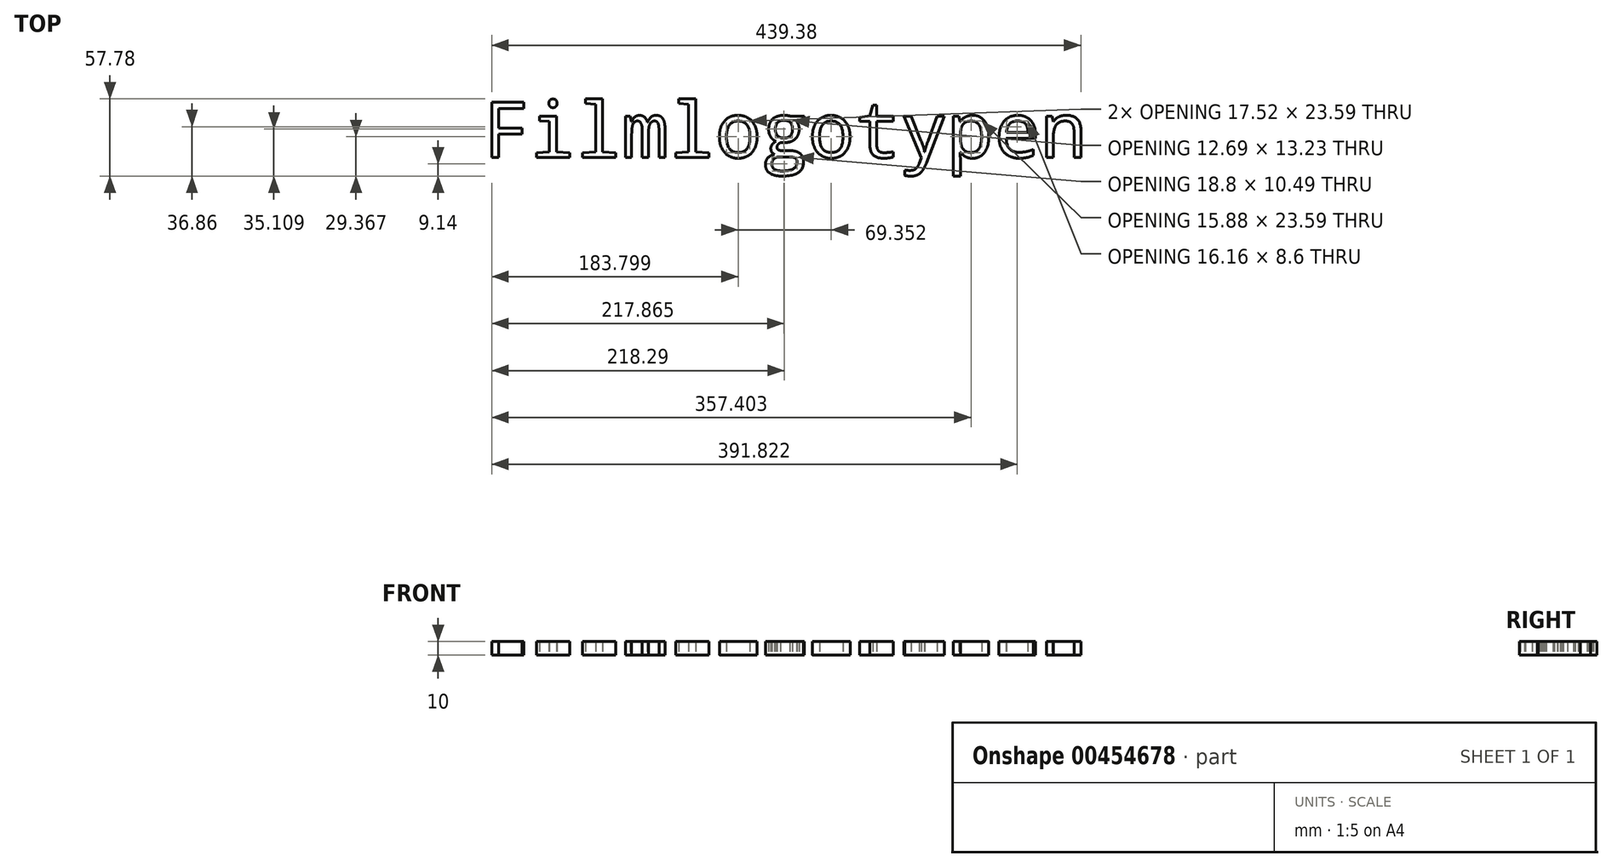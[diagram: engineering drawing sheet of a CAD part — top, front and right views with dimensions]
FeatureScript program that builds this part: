
annotation { "Feature Type Name" : "Feature", "Feature Type Description" : "" }
export const myFeature = defineFeature(function(context is Context, id is Id, definition is map)
    precondition{}
    {
        {
            var Q0;
            Q0=qCreatedBy(makeId("Top.planeOp"),FACE);
            var sketch = newSketch(context, id + "F0", { "sketchPlane" : qUnion([Q0])});
            skText(sketch, "E0", { "text": "Filmlogotypen", "fontName": "DroidSansMono.ttf"});
            const initialGuessF0  = {"E0": [-0.2141, -0.01987, 1, 0, 0.0416]};
            skSetInitialGuess(sketch, initialGuessF0);
            skSolve(sketch);
        }
        {
            var Q0;
            Q0 = qSketchRegion(id + "F0", true);
            extrude(context, id + "F1", {"entities" : qUnion([Q0]), "depth" : 10 * mm});
        }
    });
